# Revit family: Floors_Floor-Construction-Pedestal_Buzon_BC-9
name_source: partatom
category: Generic Models
revit_build: Autodesk Revit 2015 (Build: 20140606_1530(x64)
units: mm (PartAtom-declared; Revit-internal decimal feet)

## types (1)
- BC 9
    BIMobject category = Systems
    Brand url = http://www.buzon-world.com
    Default Elevation = 1219 mm
    Description = Buzon Pedestal International is the first and leading European manufacturer of adjustable pedestals for raised floorings and terraces, such as roof and landscape areas, water features, balconies, pool decks, walkways, showrooms, exhibition areas, etc.Buzon screw-jack pedestals offer uninterrupted adjustability, are made from 78% recycled and 100% recyclable polypropylene. They can be adjusted to compensate for up to 5%
pitch, or compensate for locally uneven sub-bases up to the same amount.
Once pedestals are at the required height, their position is fixed with unique lockable keys. The slope corrector BC-PH5(8) can compensate a slope from 0 to 5% (slope from 0 to 5 cm per meter). This is placed under the base of the pedestal.
    Design country = Belgium
    Edition number = 1
    IFC Classification = Building Element
    Manufacturer country = Belgium
    Manufacturer name = Buzon
    Material main = Polypropylene
    Material secondary = Polypropylene
    Model = BC 9
    NBS Reference Code = 20-20
    NBS Reference Description = Flooring And Decking Systems
    Nominal height = 0 mm  [stored 0 ft]
    Nominal width = 0 mm  [stored 0 ft]
    OmniClass Code = 23-15 17 11
    OmniClass Description = Flooring Specialties and Accessories
    Pedestal Material = Default_BC-8_Material
    Product Guid = 49f8765e-703f-4591-b121-78581e5fa3cb
    Product Material = Default_BC-8_Material
    Product SKU = BC-9
    Product data url = https://bimobject.com
    Product family = BC
    Product group = Pedestal
    Product url = http://www.buzon-world.com
    QR code = http://bimobject.com
    UNSPSC Code = 301617
    Uniclass 1.4 Code = L83121
    Uniclass 1.4 Description = Floor units
    Uniclass 2.0 Code = SS-20-20
    Uniclass 2.0 Description = Flooring And Decking Systems
    Uniclass 2015 Code = Ss_30_42_32_30
    Uniclass 2015 Name = External floor tiling systems
    Uniformat II Code = B1010
    Uniformat II Description = Floor Construction
    Weight Net (Kg) = 0

note: [stored X ft] marks values corroborated as IEEE doubles in the binary element streams (Revit-internal decimal feet)

## geometry (parser evidence)
native form markers: Blend x4, Sweep x25
no freeform markers — native parametric forms only
